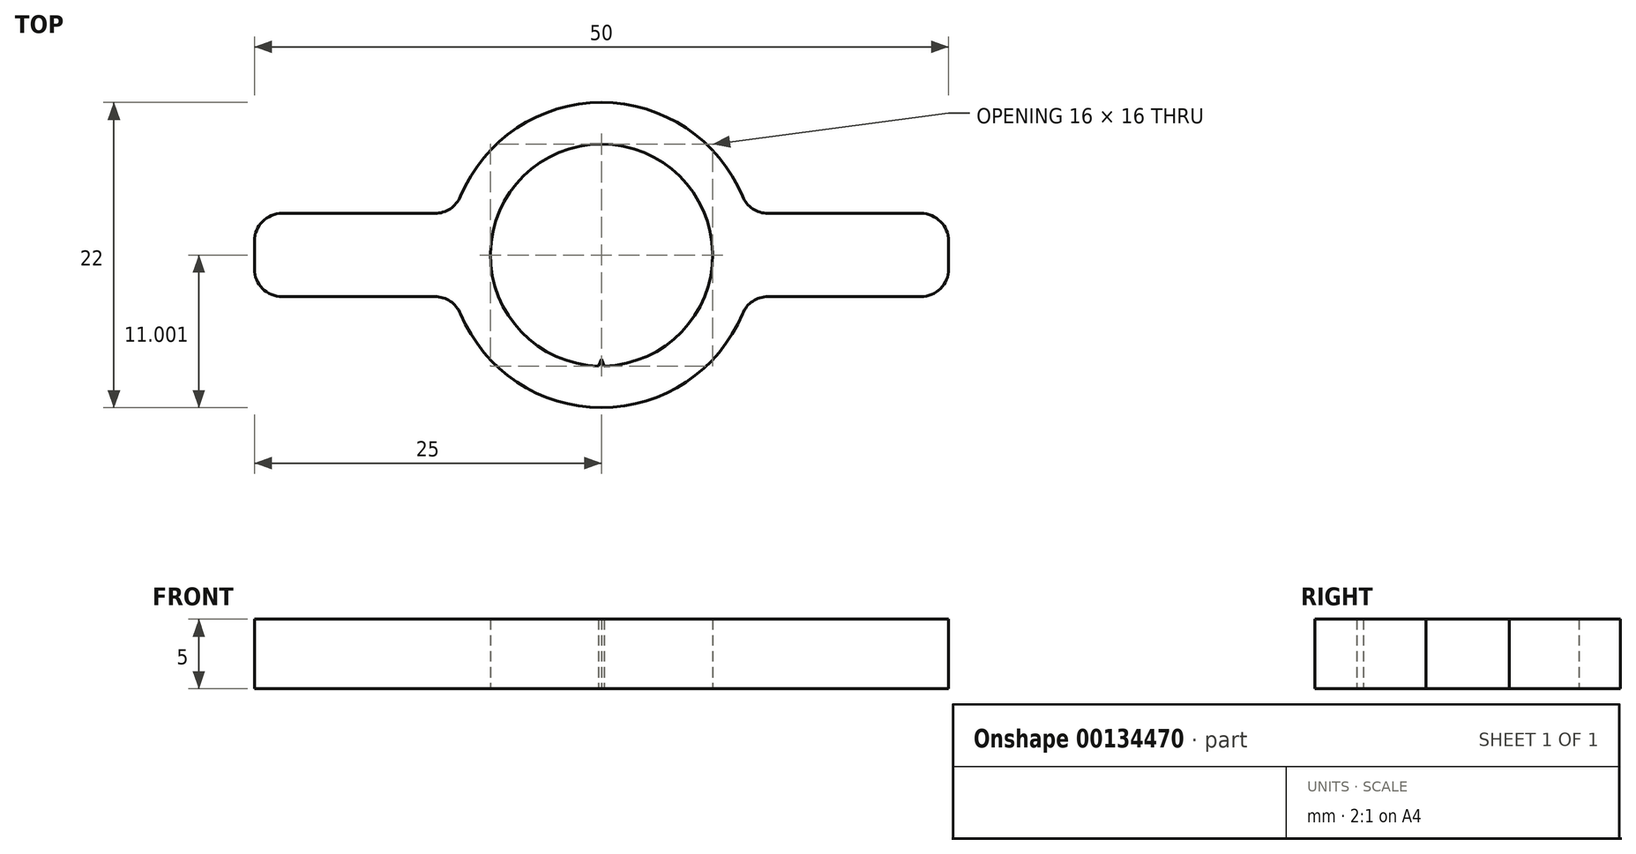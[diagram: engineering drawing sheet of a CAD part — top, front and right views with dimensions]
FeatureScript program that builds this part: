
annotation { "Feature Type Name" : "Feature", "Feature Type Description" : "" }
export const myFeature = defineFeature(function(context is Context, id is Id, definition is map)
    precondition{}
    {
        {
            var Q0;
            Q0=qCreatedBy(makeId("Top.planeOp"),FACE);
            var sketch = newSketch(context, id + "F0", { "sketchPlane" : qUnion([Q0])});
            skCircle(sketch, "E0", {"center": v(0, 0) * mm, "radius": 8 * mm});
            skArc(sketch, "E1", {"start": v(-10.58, -3) * mm, "mid": v(0, -11) * mm, "end": v(10.58, -3) * mm});
            skLineSegment(sketch, "E2.bottom", {"start": v(25, -3) * mm, "end": v(10.58, -3) * mm});
            skLineSegment(sketch, "E2.top", {"start": v(25, 3) * mm, "end": v(10.58, 3) * mm});
            skLineSegment(sketch, "E2.left", {"start": v(25, -3) * mm, "end": v(25, 3) * mm});
            skLineSegment(sketch, "E2.right", {"start": v(-25, -3) * mm, "end": v(-25, 3) * mm});
            skLineSegment(sketch, "E3.trimOffspring", {"start": v(-10.58, 3) * mm, "end": v(-25, 3) * mm});
            skLineSegment(sketch, "E4.trimOffspring", {"start": v(-10.58, -3) * mm, "end": v(-25, -3) * mm});
            skArc(sketch, "E5.trimOffspring", {"start": v(10.58, 3) * mm, "mid": v(0, 11) * mm, "end": v(-10.58, 3) * mm});
            skSolve(sketch);
        }
        {
            var Q0;
            Q0=makeQuery(id+"F0.imprint","IMPRINT",FACE,{"disambiguationData":[TD([[makeQuery(id+"F0.imprint","IMPRINT",EDGE,{"derivedFrom":sQuery(id+"F0.wireOp",EDGE,"E0")}),-1.0]])]});
            extrude(context, id + "F1", {"entities" : qUnion([Q0]), "depth" : 5 * mm});
        }
        {
            var Q0;
            Q0=qCreatedBy(makeId("Top.planeOp"),FACE);
            var sketch = newSketch(context, id + "F2", { "sketchPlane" : qUnion([Q0])});
            skLineSegment(sketch, "E6", {"start": v(-0.2, -8) * mm, "end": v(0, -7.5) * mm});
            skLineSegment(sketch, "E7", {"start": v(0, -7.5) * mm, "end": v(0.2, -8) * mm});
            skArc(sketch, "E8.0", {"start": v(-0.2, -8) * mm, "mid": v(0, -8) * mm, "end": v(0.2, -8) * mm});
            skSolve(sketch);
        }
        {
            var Q0;
            Q0 = qSketchRegion(id + "F2", true);
            extrude(context, id + "F3", {"entities" : qUnion([Q0]), "operationType" : NewBodyOperationType.ADD, "depth" : 5 * mm});
        }
        {
            var Q0;
            Q0=makeQuery(id+"F1.opExtrude","SWEPT_EDGE",EDGE,{"disambiguationData":[OSD([sQuery(id+"F0.wireOp",EDGE,"E2.right"),sQuery(id+"F0.wireOp",EDGE,"E3.trimOffspring")])]});
            var Q1;
            Q1=makeQuery(id+"F1.opExtrude","SWEPT_EDGE",EDGE,{"disambiguationData":[OSD([sQuery(id+"F0.wireOp",EDGE,"E2.right"),sQuery(id+"F0.wireOp",EDGE,"E4.trimOffspring")])]});
            var Q2;
            Q2=makeQuery(id+"F1.opExtrude","SWEPT_EDGE",EDGE,{"disambiguationData":[OSD([sQuery(id+"F0.wireOp",EDGE,"E2.top"),sQuery(id+"F0.wireOp",EDGE,"E2.left")])]});
            var Q3;
            Q3=makeQuery(id+"F1.opExtrude","SWEPT_EDGE",EDGE,{"disambiguationData":[OSD([sQuery(id+"F0.wireOp",EDGE,"E3.trimOffspring"),sQuery(id+"F0.wireOp",EDGE,"E5.trimOffspring")])]});
            var Q4;
            Q4=makeQuery(id+"F1.opExtrude","SWEPT_EDGE",EDGE,{"disambiguationData":[OSD([sQuery(id+"F0.wireOp",EDGE,"E2.bottom"),sQuery(id+"F0.wireOp",EDGE,"E2.left")])]});
            var Q5;
            Q5=makeQuery(id+"F1.opExtrude","SWEPT_EDGE",EDGE,{"disambiguationData":[OSD([sQuery(id+"F0.wireOp",EDGE,"E1"),sQuery(id+"F0.wireOp",EDGE,"E2.bottom")])]});
            var Q6;
            Q6=makeQuery(id+"F1.opExtrude","SWEPT_EDGE",EDGE,{"disambiguationData":[OSD([sQuery(id+"F0.wireOp",EDGE,"E1"),sQuery(id+"F0.wireOp",EDGE,"E4.trimOffspring")])]});
            var Q7;
            Q7=makeQuery(id+"F1.opExtrude","SWEPT_EDGE",EDGE,{"disambiguationData":[OSD([sQuery(id+"F0.wireOp",EDGE,"E2.top"),sQuery(id+"F0.wireOp",EDGE,"E5.trimOffspring")])]});
            fillet(context, id + "F4", {"entities" : qUnion([Q0, Q1, Q2, Q3, Q4, Q5, Q6, Q7]), "radius" : 2 * mm, "tangentPropagation" : true, "allowEdgeOverflow" : false});
        }
    });
